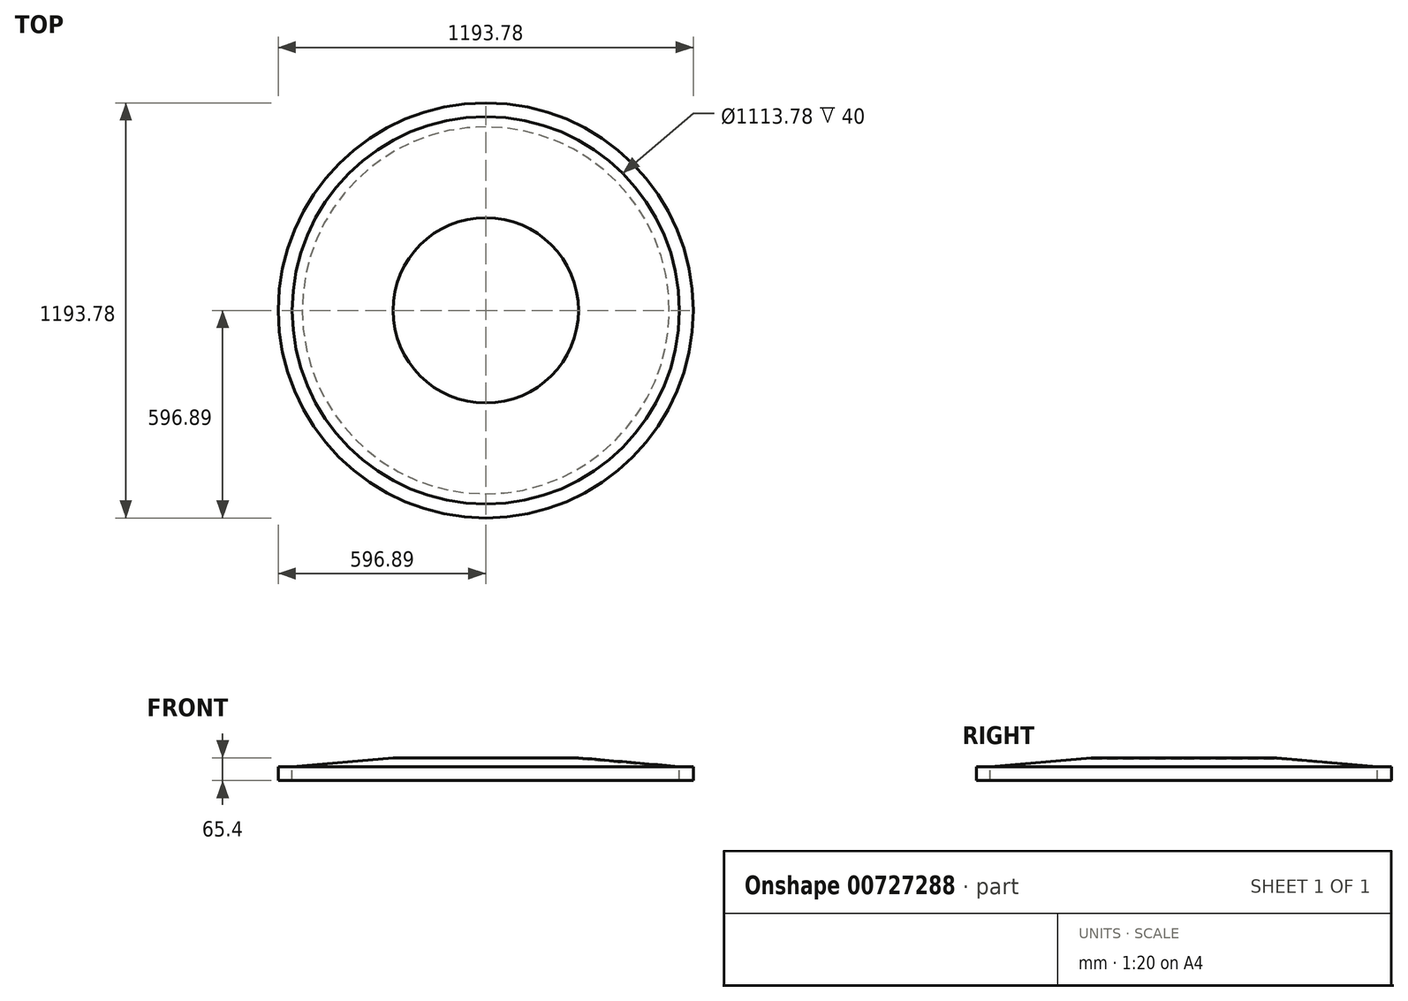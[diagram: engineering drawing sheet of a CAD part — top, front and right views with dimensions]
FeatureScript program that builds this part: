
annotation { "Feature Type Name" : "Feature", "Feature Type Description" : "" }
export const myFeature = defineFeature(function(context is Context, id is Id, definition is map)
    precondition{}
    {
        {
            var Q0;
            Q0=qCreatedBy(makeId("Top.planeOp"),FACE);
            var sketch = newSketch(context, id + "F0", { "sketchPlane" : qUnion([Q0])});
            skCircle(sketch, "E0", {"center": v(0, 0) * mm, "radius": 596.9 * mm});
            skSolve(sketch);
        }
        {
            var Q0;
            Q0 = qSketchRegion(id + "F0", true);
            extrude(context, id + "F1", {"entities" : qUnion([Q0]), "depth" : 40 * mm, "offsetDistance" : 25.4 * mm});
        }
        {
            var Q0;
            Q0=makeQuery(id+"F1.opExtrude","CAP_FACE",FACE,{"disambiguationData":[OSD([sQuery(id+"F0.wireOp",EDGE,"E0")])],"isStart":false});
            var sketch = newSketch(context, id + "F2", { "sketchPlane" : qUnion([Q0])});
            skCircle(sketch, "E1", {"center": v(0, 0) * mm, "radius": 556.9 * mm});
            skSolve(sketch);
        }
        {
            var Q0;
            Q0 = qSketchRegion(id + "F2", true);
            extrude(context, id + "F3", {"entities" : qUnion([Q0]), "operationType" : NewBodyOperationType.REMOVE, "oppositeDirection" : true, "depth" : 154.94 * mm, "offsetDistance" : 25.4 * mm});
        }
        {
            var Q0;
            Q0=makeQuery(id+"F1.opExtrude","CAP_FACE",FACE,{"disambiguationData":[OSD([sQuery(id+"F0.wireOp",EDGE,"E0")])],"isStart":false});
            var sketch = newSketch(context, id + "F4", { "sketchPlane" : qUnion([Q0])});
            skCircle(sketch, "E2", {"center": v(0, 0) * mm, "radius": 556.9 * mm});
            skSolve(sketch);
        }
        {
            var Q0;
            Q0 = qSketchRegion(id + "F4", true);
            extrude(context, id + "F5", {"entities" : qUnion([Q0]), "depth" : 25.4 * mm, "offsetDistance" : 25.4 * mm, "hasDraft" : true, "draftAngle" : 85 * degree, "draftPullDirection" : true});
        }
        {
            var Q0;
            Q0=makeQuery(id+"F5.opExtrude","CAP_FACE",FACE,{"disambiguationData":[OSD([sQuery(id+"F4.wireOp",EDGE,"E2")])],"isStart":true});
            shell(context, id + "F6", {"entities" : qUnion([Q0]), "thickness" : 2.54 * mm});
        }
    });
